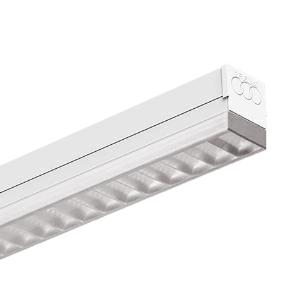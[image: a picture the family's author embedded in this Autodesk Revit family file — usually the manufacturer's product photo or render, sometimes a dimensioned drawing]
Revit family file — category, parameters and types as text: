
# Revit family: 3f_filippi_-_3f_zeta_dr_ugr_3f_filippi_-_10594_-_3f_zeta_dr_ugr_1x24_led_dali_l1194
name_source: partatom
category: Lighting Fixtures
units: mm (PartAtom-declared; Revit-internal decimal feet)

## family parameters
Cut with Voids When Loaded = No
Host = Face
Light Source = No
Part Type = Normal
Room Calculation Point = No
Round Connector Dimension = Use Diameter
Shared = No

## types (1)
- 3F Filippi - 3F Zeta DR UGR (1 x LED, 2786 lm, 27 W, 4000 K)
    Apparent Load = 27 VA
    Approval mark = CE
    CIE Flux Codes = 69 97 100 100 100
    Color Rendering = 80
    Color Temperature = 4000 K
    Control Gear = Electronic transformer
    Default Elevation = 1800 mm
    Description = ILLUMINOTECHNICAL
Luminous efficiency 100% (DLOR 99%, ULOR 1%).
Initial luminous flux of the luminaire 2786 lm.
Controlled direct symmetric distribution.
Installation Interdistance Transv.D = 1.38 x hu - Long.D = 1.25 x hu.
Average luminance <3000 cd/m² for radial angles >65°.
Tabular UGR (CIE 117 - 4H-8H; S=0.25H; 70/50/20): RUG 17.2 - 18.6.
Beam angle: 87° - 91°.
Luminous efficacy 103 lm/W.
Lifetime (L93/B10): 30000 h. (tq+25°C)
Lifetime (L90/B10): 50000 h. (tq+25°C)
Lifetime (L85/B10): 80000 h. (tq+25°C)
Lifetime (L80/B10): 100000 h. (tq+25°C)
Sudden decreased luminous flux after 50000 hours: 0% (C0).
Photobiological safety in compliance with IEC/TR 62778: RG0 risk exempt, (IEC 62471).
In compliance with IEC/EN 62722-2-1 - IEC/EN 62717 standards.

SOURCE
Linear LED module 24W/840.
Energy efficiency class (UE 2019/2020 - UE 2019/2015): D.
CIE 13.3 Colour rendering index: CRI >80 (R9 <50%).
IES TM-30 Fidelity Index: Rf = 84 Rg = 95.
CCT nominal colour temperature 4000 K.
Colour initial tolerance (MacAdam): SDCM 3.

MECHANICAL
Housing in hot-galvanised steel, painted in white polyester, obtained through rolling process.
Light unit in hot-galvanised steel, painted in white polyester base with fixing springs and retractable safety hooks in stainless steel.
Semi-specular aluminium internal louvre with prismatic methacrylate (PMMA) filter above the louvre blades for complete shielding of the louvre compartment.
Rectangular screen in self-extinguishing polycarbonate, UV stabilised, transparent, with smooth outer surface.
End caps in white polycarbonate.
Pair of stainless steel sliding brackets with sliding block screws.
Luminaire with limited surface temperature. - D - (EN 60598-2-24)
Dimensions: 1194x62 mm, height 81 mm. Weight 3.3 kg.
IP40 protection degree.
Mechanical strength to impacts IK06 (1 joule).
Glow-wire test resistance 850°C.

ELECTRICAL
Halogen Free DALI-2 DATI (Parts 251, 252, 253), PUSH-DIM, electronic wiring 230V-50/60Hz, power factor 0.90 at full load, THD <25%, constant output current, SELV, class I, 1 driver, 1 DALI addresse.
Power of the luminaire 27 W.
ENEC - CE.
SAFE FLICKER: PstLM=<1 and SVM=<0.4 (IEC TR 61547-1 and IEC TR 63158), to ensure a more comfortable and safe light.
Luminaire compliant with EN 60598-2-22 for power supply from a centralised emergency system CPSS (Central Power Supply System), not incorporated in the luminaire - high risk areas excluded. The default power and flux are 100% in AC and 15% in DC.
Ambient temperature from 0°C to +25°C.
Temperature class T6 max 85°C.
Relative humidity UR: <85%.

INSTALLATION
Ceiling / Suspended / Wall.
All accessories dedicated to this product are available on the Catalog and on our website www.3F-Filippi.com.

APPLICATIONS
Suitable product for food production plants (HACCP), IFS (Food Version 6), BRC (GSFS Food Version 7).
In environments with VDTs, managerial offices and staterooms, public offices and schools.

LIGHT MANAGEMENT
Recommended minimum setting: 10%.
The luminaire, equipped with (DALI-2 DATI) driver, can be controlled manually with 3F Easy Dim technology or automatically/manually with wired or wireless DALI/D2D control systems.
The D2D driver guarantees interoperability with other devices with the same certification by making the following information available:
Device Data (Part 251), Energy Report (Part 252), Diagnosis & Maintenance (Part 253).
In electrical systems without a regulation system (manual or automatic) and DALI bus, a suitable jumper must be made on the DA-DA terminals of the appliance.

WARNING
Luminaire designed for disposal/recycling at end-of-life.
Replaceable (LED only) light source by a professional. Replaceable control gear by a professional.
    Height = 81 mm
    Lamp = 1 x LED
    Lamp Light Flux = 2786 lm
    Lamp Power = 27 W
    Lamp count = 1
    Length = 1194 mm
    Lifetime = 50000 h
    Luminous efficacy = 103 lm/W
    Manufacturer = 3F Filippi
    ModVariant = No
    Model = 3F Filippi - 10594 - 3F Zeta DR UGR 1x24 LED DALI L1194
    Mounting Place = Ceiling
    Mounting Type = Surface mounted
    Number of Poles = 1
    OnlyDefault = Yes
    Power Factor = 1
    Product Name = 3F Filippi - 3F Zeta DR UGR
    Product group = ceiling mounted luminaire
    ProductGroupID = 3
    Protection Class = Protection class I
    Protection Degree = IP 40
    RLX_Detail_Level = 1
    RLX_Emergency_Light_Flux = 0 lm
    RLX_Emergency_Type = 0
    RLX_Emergency_Type_DB = No
    RlxData = <blob elided: 49877 chars, md5=3577680b>
    Socket = socket
    Standby Power = 0 W
    System Light Flux = 2786 lm
    System Power = 27 W
    Type Comments = Product without accessories
    Type Image = 3ffilippi_3f_zeta_dr_ugr.jpg
    URL = http://relux.com
    VarID = ---
    Voltage = 0 V
    Weight = 0.00 kg
    Width = 62 mm

## geometry (parser evidence)
native form markers: Blend x4, Sweep x11
no freeform markers — native parametric forms only
